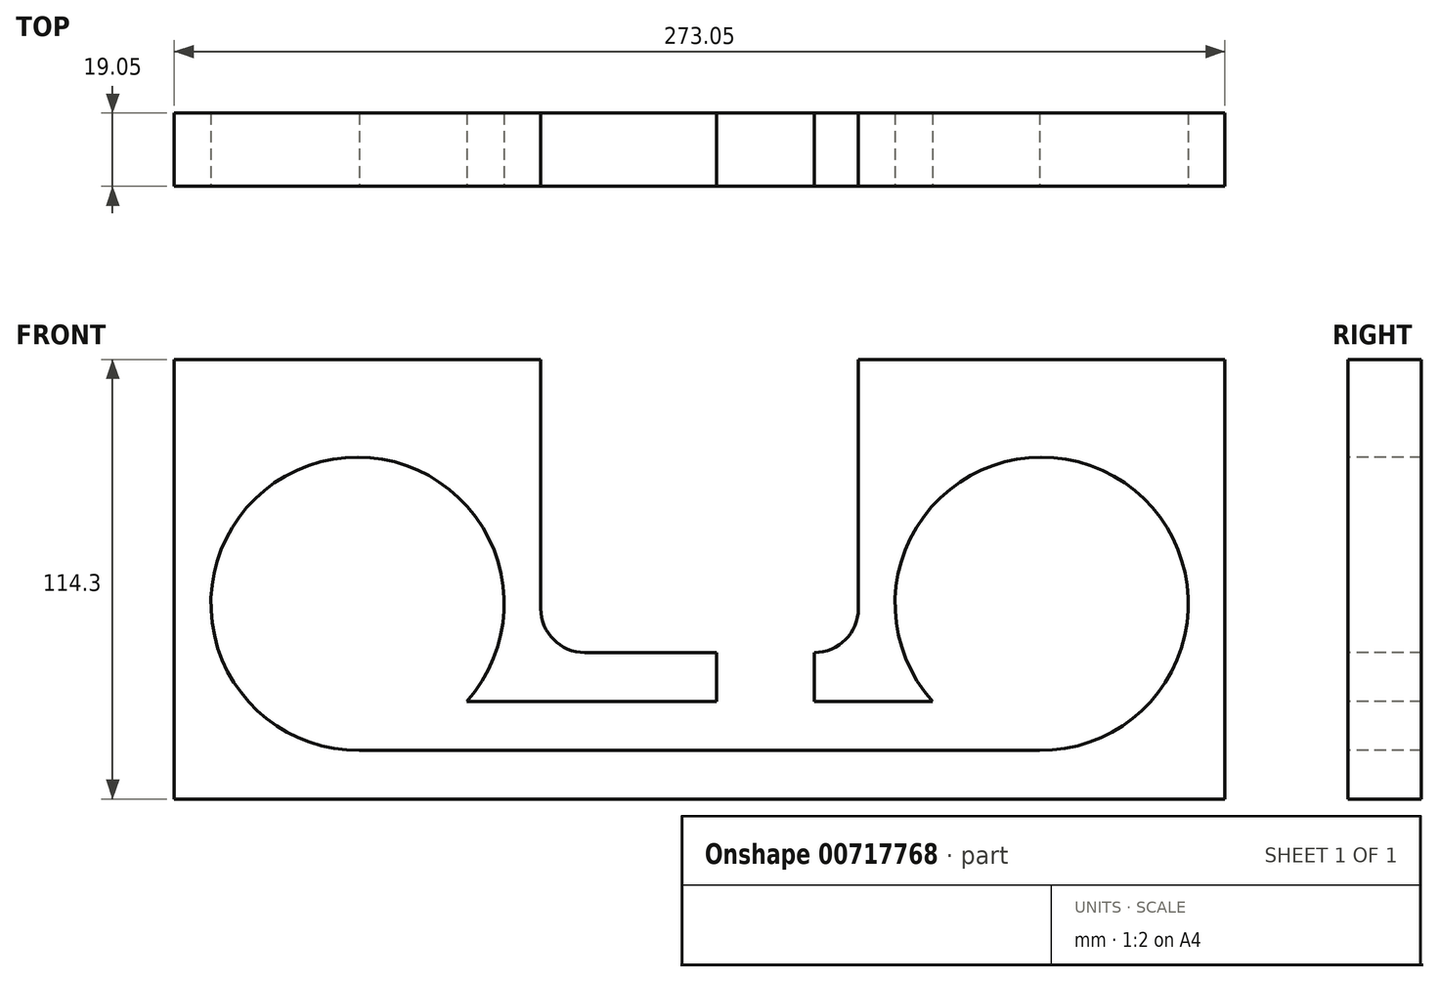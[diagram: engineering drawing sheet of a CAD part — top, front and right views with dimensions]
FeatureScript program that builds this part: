
annotation { "Feature Type Name" : "Feature", "Feature Type Description" : "" }
export const myFeature = defineFeature(function(context is Context, id is Id, definition is map)
    precondition{}
    {
        {
            var Q0;
            Q0=qCreatedBy(makeId("Front.planeOp"),FACE);
            var sketch = newSketch(context, id + "F0", { "sketchPlane" : qUnion([Q0])});
            skLineSegment(sketch, "E0.bottom", {"start": v(0, 0) * mm, "end": v(273.05, 0) * mm});
            skLineSegment(sketch, "E0.top", {"start": v(0, 114.3) * mm, "end": v(273.05, 114.3) * mm});
            skLineSegment(sketch, "E0.left", {"start": v(0, 0) * mm, "end": v(0, 114.3) * mm});
            skLineSegment(sketch, "E0.right", {"start": v(273.05, 0) * mm, "end": v(273.05, 114.3) * mm});
            skSolve(sketch);
        }
        {
            var Q0;
            Q0 = qSketchRegion(id + "F0", true);
            extrude(context, id + "F1", {"entities" : qUnion([Q0]), "depth" : 19.05 * mm, "offsetDistance" : 25.4 * mm});
        }
        {
            var Q0;
            Q0=makeQuery(id+"F1.opExtrude","CAP_FACE",FACE,{"disambiguationData":[OSD([sQuery(id+"F0.wireOp",EDGE,"E0.bottom"),sQuery(id+"F0.wireOp",EDGE,"E0.top"),sQuery(id+"F0.wireOp",EDGE,"E0.left"),sQuery(id+"F0.wireOp",EDGE,"E0.right")])],"isStart":false});
            var sketch = newSketch(context, id + "F2", { "sketchPlane" : qUnion([Q0])});
            skCircle(sketch, "E1", {"center": v(47.63, 50.8) * mm, "radius": 38.1 * mm});
            skCircle(sketch, "E2", {"center": v(225.43, 50.8) * mm, "radius": 38.1 * mm});
            skPoint(sketch, "E2.centerSnap0", {"position": v(273.05, 50.8) * mm});
            skSolve(sketch);
        }
        {
            var Q0;
            Q0=makeQuery(id+"F2.imprint","IMPRINT",FACE,{"disambiguationData":[TD([[makeQuery(id+"F2.imprint","IMPRINT",EDGE,{"derivedFrom":sQuery(id+"F2.wireOp",EDGE,"E1")}),1.0]])]});
            var Q1;
            Q1=makeQuery(id+"F2.imprint","IMPRINT",FACE,{"disambiguationData":[TD([[makeQuery(id+"F2.imprint","IMPRINT",EDGE,{"derivedFrom":sQuery(id+"F2.wireOp",EDGE,"E2")}),1.0]])]});
            extrude(context, id + "F3", {"entities" : qUnion([Q0, Q1]), "operationType" : NewBodyOperationType.REMOVE, "oppositeDirection" : true, "depth" : 25.4 * mm, "offsetDistance" : 25.4 * mm});
        }
        {
            var Q0;
            Q0=makeQuery(id+"F1.opExtrude","CAP_FACE",FACE,{"disambiguationData":[OSD([sQuery(id+"F0.wireOp",EDGE,"E0.bottom"),sQuery(id+"F0.wireOp",EDGE,"E0.top"),sQuery(id+"F0.wireOp",EDGE,"E0.left"),sQuery(id+"F0.wireOp",EDGE,"E0.right")])],"isStart":false});
            var sketch = newSketch(context, id + "F4", { "sketchPlane" : qUnion([Q0])});
            skLineSegment(sketch, "E3.bottom", {"start": v(95.25, 114.3) * mm, "end": v(177.8, 114.3) * mm});
            skLineSegment(sketch, "E3.top", {"start": v(106.68, 38.1) * mm, "end": v(166.37, 38.1) * mm});
            skLineSegment(sketch, "E3.left", {"start": v(95.25, 114.3) * mm, "end": v(95.25, 49.53) * mm});
            skLineSegment(sketch, "E3.right", {"start": v(177.8, 114.3) * mm, "end": v(177.8, 49.53) * mm});
            skPoint(sketch, "E4.visualSharp", {"position": v(95.25, 38.1) * mm});
            skArc(sketch, "E4.filletArc", {"start": v(95.25, 49.53) * mm, "mid": v(98.6, 41.45) * mm, "end": v(106.68, 38.1) * mm});
            skPoint(sketch, "E5.visualSharp", {"position": v(177.8, 38.1) * mm});
            skArc(sketch, "E5.filletArc", {"start": v(166.37, 38.1) * mm, "mid": v(174.45, 41.45) * mm, "end": v(177.8, 49.53) * mm});
            skSolve(sketch);
        }
        {
            var Q0;
            Q0=makeQuery(id+"F4.imprint","IMPRINT",FACE,{"disambiguationData":[TD([[makeQuery(id+"F4.imprint","IMPRINT",EDGE,{"derivedFrom":sQuery(id+"F4.wireOp",EDGE,"E3.bottom")}),-1.0]])]});
            extrude(context, id + "F5", {"entities" : qUnion([Q0]), "operationType" : NewBodyOperationType.REMOVE, "oppositeDirection" : true, "depth" : 25.4 * mm, "offsetDistance" : 25.4 * mm});
        }
        {
            var Q0;
            Q0=makeQuery(id+"F1.opExtrude","CAP_FACE",FACE,{"disambiguationData":[OSD([sQuery(id+"F0.wireOp",EDGE,"E0.bottom"),sQuery(id+"F0.wireOp",EDGE,"E0.top"),sQuery(id+"F0.wireOp",EDGE,"E0.left"),sQuery(id+"F0.wireOp",EDGE,"E0.right")])],"isStart":false});
            var sketch = newSketch(context, id + "F6", { "sketchPlane" : qUnion([Q0])});
            skLineSegment(sketch, "E6", {"start": v(166.37, 38.1) * mm, "end": v(140.97, 38.1) * mm});
            skLineSegment(sketch, "E7", {"start": v(140.97, 38.1) * mm, "end": v(140.97, 25.4) * mm});
            skLineSegment(sketch, "E8", {"start": v(140.97, 25.4) * mm, "end": v(76.03, 25.4) * mm});
            skLineSegment(sketch, "E9", {"start": v(76.03, 25.4) * mm, "end": v(47.1, 12.7) * mm});
            skLineSegment(sketch, "E10", {"start": v(47.1, 12.7) * mm, "end": v(225.95, 12.7) * mm});
            skLineSegment(sketch, "E11", {"start": v(225.95, 12.7) * mm, "end": v(197.02, 25.4) * mm});
            skLineSegment(sketch, "E12", {"start": v(197.02, 25.4) * mm, "end": v(166.37, 25.4) * mm});
            skLineSegment(sketch, "E13", {"start": v(166.37, 25.4) * mm, "end": v(166.37, 38.1) * mm});
            skSolve(sketch);
        }
        {
            var Q0;
            Q0=makeQuery(id+"F6.imprint","IMPRINT",FACE,{"disambiguationData":[TD([[makeQuery(id+"F6.imprint","IMPRINT",EDGE,{"derivedFrom":sQuery(id+"F6.wireOp",EDGE,"E6")}),-1.0]])]});
            extrude(context, id + "F7", {"entities" : qUnion([Q0]), "operationType" : NewBodyOperationType.REMOVE, "oppositeDirection" : true, "depth" : 25.4 * mm, "offsetDistance" : 25.4 * mm});
        }
    });
